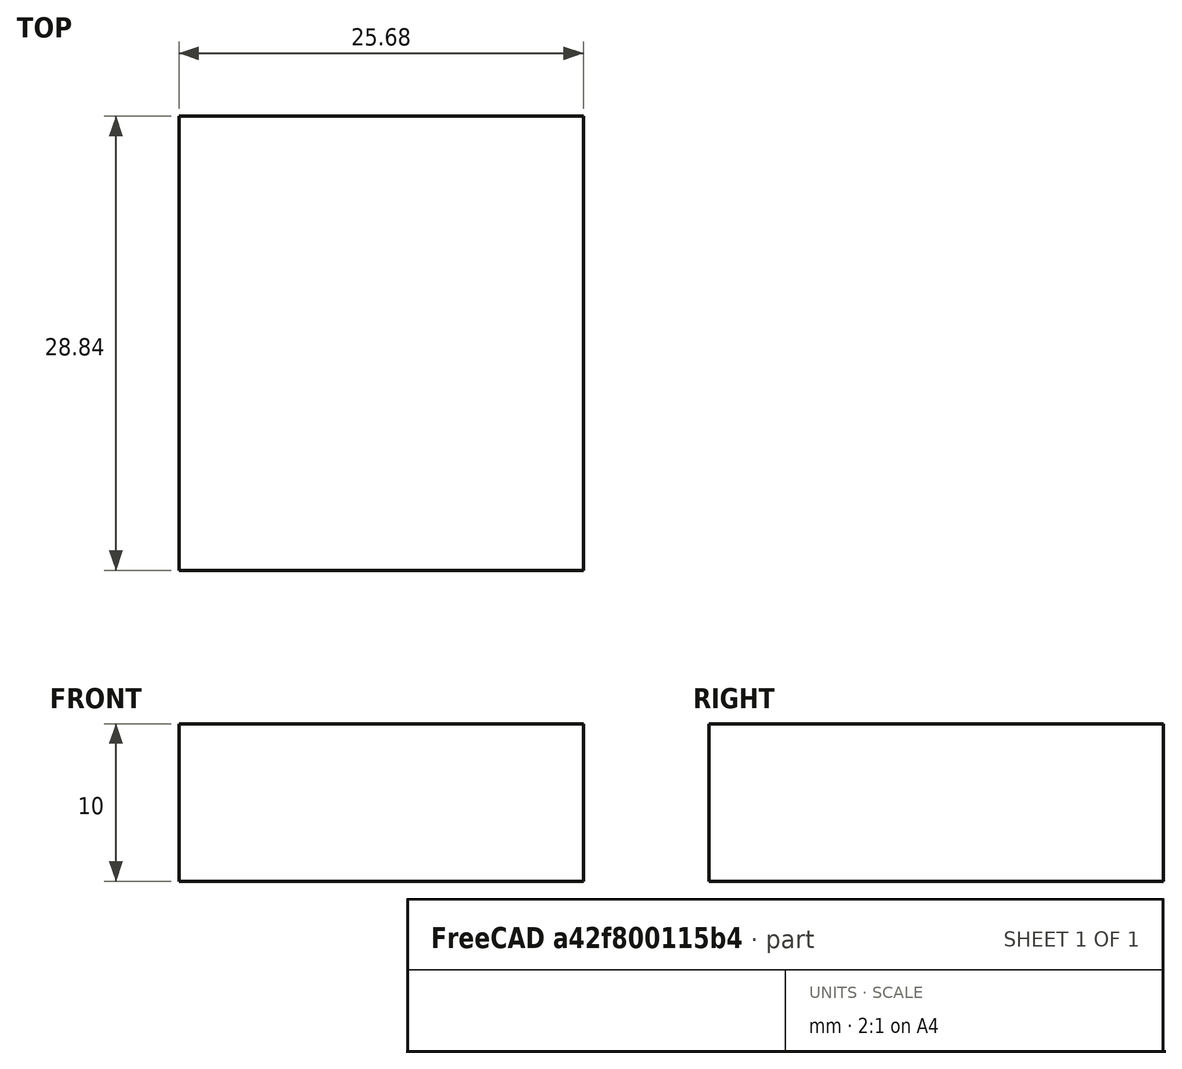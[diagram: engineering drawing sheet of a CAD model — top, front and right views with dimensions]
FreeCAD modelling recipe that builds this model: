
FCSTD DOCUMENT  (FreeCAD 1.1R14555 (Git shallow))
Label: TestInsertLink1-1
License: All rights reserved
LicenseURL: https://en.wikipedia.org/wiki/All_rights_reserved
objects: App::Link×8, App::Point×4, Assembly::AssemblyLink×2, App::FeaturePython×2, Sketcher::SketchObject×1, PartDesign::Pad×1, PartDesign::Body×1, Assembly::JointGroup×1, Assembly::AssemblyObject×1
note: 6 computed .brp shape members not serialized (recipe doc carries the construction recipe); baked Part::Feature solids carry a one-line shape summary decoded from their .brp
EXTERNAL_REF file=TestMeca1-1.FCStd obj=Assembly
EXTERNAL_REF file=TestMeca1-1.FCStd obj=Body
EXTERNAL_REF file=TestMeca1-1.FCStd obj=Body001
EXTERNAL_REF file=TestMeca1-1.FCStd obj=Body002
EXTERNAL_REF file=TestMeca1-1.FCStd obj=Body004
EXTERNAL_REF file=TestMeca1-1.FCStd obj=Body005
EXTERNAL_REF file=TestMeca1-1.FCStd obj=Assembly001
EXTERNAL_REF file=TestMeca1-1.FCStd obj=Assembly002
EXTERNAL_REF file=TestInsert1-1.FCStd obj=Body
EXTERNAL_REF file=TestInsert1-1.FCStd obj=Body001

FEATURE [App::Point] Origin001  label="Origine"
  Role = Origin
FEATURE [App::Point] Origin003  label="Origine002"
  Role = Origin
FEATURE [App::Link] Body  label="Corps"
  LinkedObject = -> <external TestMeca1-1.FCStd>#Body
FEATURE [App::Link] Body001  label="Corps001"
  LinkPlacement = pos=(-5.08123,5,5.38487) rot=(0,1,0;0.743384rad)
  LinkedObject = -> <external TestMeca1-1.FCStd>#Body001
  Placement = pos=(-5.08123,5,5.38487) rot=(0,1,0;0.743384rad)
FEATURE [App::Link] Body002  label="Corps002"
  LinkPlacement = pos=(67.6695,10,-11.2681) rot=(0,-1,0;0.15337rad)
  LinkedObject = -> <external TestMeca1-1.FCStd>#Body002
  Placement = pos=(67.6695,10,-11.2681) rot=(0,-1,0;0.15337rad)
FEATURE [App::Link] Body004  label="Corps004"
  LinkPlacement = pos=(40.5944,10,0.68856) rot=(0,-1,0;0.161439rad)
  LinkedObject = -> <external TestMeca1-1.FCStd>#Body004
  Placement = pos=(40.5944,10,0.68856) rot=(0,-1,0;0.161439rad)
FEATURE [App::Link] Body005  label="Corps005"
  LinkPlacement = pos=(5.56671,5,23.7456) rot=(0,1,0;0.882835rad)
  LinkedObject = -> <external TestMeca1-1.FCStd>#Body005
  Placement = pos=(5.56671,5,23.7456) rot=(0,1,0;0.882835rad)
FEATURE [App::Link] Assembly002  label="Assembly001"
  LinkPlacement = pos=(-34.0984,5.00001,62.3122) rot=(0,1,0;0.514812rad)
  LinkedObject = -> <external TestMeca1-1.FCStd>#Assembly001
  Placement = pos=(-34.0984,5.00001,62.3122) rot=(0,1,0;0.514812rad)
FEATURE [App::Point] Origin005  label="Origine004"
  Role = Origin
FEATURE [App::Link] Body006  label="Corps006"
  LinkedObject = -> <external TestInsert1-1.FCStd>#Body
FEATURE [App::Link] Body007  label="Corps007"
  LinkPlacement = pos=(-4.1e-15,3.6e-15,-4.7e-15) rot=(0,-1,0;4.71239rad)
  LinkedObject = -> <external TestInsert1-1.FCStd>#Body001
  Placement = pos=(-4.1e-15,3.6e-15,-4.7e-15) rot=(0,-1,0;4.71239rad)
FEATURE [Assembly::AssemblyLink] Assembly003  label="Assembly"
  Group = -> [Body006,Body007]
  LinkedObject = -> <external TestMeca1-1.FCStd>#Assembly002
  Origin = -> Origin004
  Placement = pos=(76.0304,-8,33.5737) rot=(0,1,0;0.730396rad)
  Rigid = true
FEATURE [Assembly::AssemblyLink] Assembly001  label="Assembly"
  Group = -> [Body,Body001,Body002,Body004,Body005,Assembly002,Assembly003]
  LinkedObject = -> <external TestMeca1-1.FCStd>#Assembly
  Origin = -> Origin002
  Placement = pos=(13.8231,8.63205,0) rot=(0,0,1;3.85382rad)
  Rigid = true
FEATURE [App::Point] Origin007  label="Origine006"
  Role = Origin
FEATURE [Sketcher::SketchObject] Sketch
  ArcFitTolerance = 1e-06
  AttachmentSupport = -> [Origin006]
  ExternalTypes = [0]
  FullyConstrained = false
  MakeInternals = false
  MapMode = 5
  sketch-geometry (5):
    g0: LineSegment StartX=12.8432 StartY=-14.4217 StartZ=0 EndX=12.8432 EndY=14.4217 EndZ=0
    g1: LineSegment StartX=12.8432 StartY=14.4217 StartZ=0 EndX=-12.8432 EndY=14.4217 EndZ=0
    g2: LineSegment StartX=-12.8432 StartY=14.4217 StartZ=0 EndX=-12.8432 EndY=-14.4217 EndZ=0
    g3: LineSegment StartX=-12.8432 StartY=-14.4217 StartZ=0 EndX=12.8432 EndY=-14.4217 EndZ=0
    g4: GeomPoint [constr] X=0 Y=0 Z=0
  constraints (10):
    c: Coincident(g0,g1)
    c: Coincident(g1,g2)
    c: Coincident(g2,g3)
    c: Coincident(g3,g0)
    c: Vertical(g0)
    c: Vertical(g2)
    c: Horizontal(g1)
    c: Horizontal(g3)
    c: Symmetric(g2,g0,g4)
    c: Coincident(g4,g-1)
FEATURE [PartDesign::Pad] Pad
  Direction = (0,0,1)
  Length = 10
  Length2 = 10
  Profile = -> Sketch
  ReferenceAxis = -> Sketch [N_Axis]
  Refine = true
  Reversed = true
  SideType = 0
  Suppressed = false
  Type = 0
  Type2 = 0
FEATURE [PartDesign::Body] Body008  label="Corps008"
  AllowCompound = false
  Group = -> [Sketch,Pad]
  Origin = -> Origin006
  Tip = -> Pad
FEATURE [App::FeaturePython] GroundedJoint  # Assembly grounded joint (typed FeaturePython)
  ObjectToGround = -> Body008
FEATURE [App::FeaturePython] Joint  label="Revolute"  # Assembly joint (typed FeaturePython)
  Angle = 0
  AngleMax = 0
  AngleMin = 0
  Detach1 = false
  Detach2 = false
  Distance = 0
  Distance2 = 0
  EnableAngleMax = false
  EnableAngleMin = false
  EnableLengthMax = false
  EnableLengthMin = false
  JointType = 1 (Revolute)
  LengthMax = 0
  LengthMin = 0
  Placement1 = pos=(-1e-16,0,0) rot=(0,0,1;0rad)
  Placement2 = pos=(16.1041,-2.5,6e-16) rot=(0,1,0;3.14159rad)
  Reference1 = -> Assembly [Body008.Face5,Body008.Face5]
  Reference2 = -> Assembly [Assembly001.Body.Face4,Assembly001.Body.Face4]
  Suppressed = false
FEATURE [Assembly::JointGroup] Joints
  Group = -> [GroundedJoint,Joint]
FEATURE [Assembly::AssemblyObject] Assembly
  Group = -> [Joints,Assembly001,Body008,GroundedJoint,Joint]
  Origin = -> Origin
  Type = Assembly

RESOLVED EXTERNAL PARTS (link-assembly join: the EXTERNAL_REF files above that resolve inside this repo's crawl, each included once):
---- part TestInsert1-1.FCStd = doc fcstd_bb9fa522eb82 ----
FCSTD DOCUMENT  (FreeCAD 1.1R14555 (Git shallow))
Label: TestInsert1-1
License: All rights reserved
LicenseURL: https://en.wikipedia.org/wiki/All_rights_reserved
objects: App::Point×3, Sketcher::SketchObject×2, PartDesign::Pad×2, PartDesign::Body×2, App::FeaturePython×1, Assembly::JointGroup×1, Assembly::AssemblyObject×1
note: 12 computed .brp shape members not serialized (recipe doc carries the construction recipe); baked Part::Feature solids carry a one-line shape summary decoded from their .brp

FEATURE [App::Point] Origin001  label="Origine"
  Role = Origin
FEATURE [App::Point] Origin003  label="Origine002"
  Role = Origin
FEATURE [Sketcher::SketchObject] Sketch
  ArcFitTolerance = 1e-06
  AttachmentSupport = -> [Origin002]
  ExternalTypes = [0]
  FullyConstrained = false
  MakeInternals = false
  MapMode = 5
  Placement = pos=(0,0,0) rot=(1,0,0;1.5708rad)
  sketch-geometry (4):
    g0: ArcOfCircle CenterX=0 CenterY=0 CenterZ=0 NormalX=0 NormalY=0 NormalZ=1 AngleXU=0 Radius=3.30838 StartAngle=2.28574 EndAngle=5.42733
    g1: ArcOfCircle CenterX=11.4427 CenterY=9.93411 CenterZ=0 NormalX=0 NormalY=0 NormalZ=1 AngleXU=0 Radius=3.30838 StartAngle=5.42733 EndAngle=8.56893
    g2: LineSegment StartX=-2.1689 StartY=2.49826 StartZ=0 EndX=9.27378 EndY=12.4324 EndZ=0
    g3: LineSegment StartX=2.1689 StartY=-2.49826 StartZ=0 EndX=13.6116 EndY=7.43585 EndZ=0
  constraints (6):
    c: Tangent(g0,g2) = 1.5708
    c: Tangent(g0,g3) = -1.5708
    c: Tangent(g1,g2) = 1.5708
    c: Tangent(g1,g3) = -1.5708
    c: Equal(g0,g1)
    c: Coincident(g0,g-1)
FEATURE [PartDesign::Pad] Pad
  Direction = (0,-1,0)
  Length = 10
  Length2 = 10
  Profile = -> Sketch
  ReferenceAxis = -> Sketch [N_Axis]
  Refine = true
  SideType = 0
  Suppressed = false
  Type = 0
  Type2 = 0
FEATURE [PartDesign::Body] Body  label="Corps"
  AllowCompound = false
  Group = -> [Sketch,Pad]
  Origin = -> Origin002
  Tip = -> Pad
FEATURE [App::Point] Origin005  label="Origine004"
  Role = Origin
FEATURE [Sketcher::SketchObject] Sketch001
  ArcFitTolerance = 1e-06
  AttachmentSupport = -> [Origin004]
  ExternalTypes = [0]
  FullyConstrained = false
  MakeInternals = false
  MapMode = 5
  Placement = pos=(0,0,0) rot=(1,0,0;1.5708rad)
  sketch-geometry (1):
    g0: Circle CenterX=0 CenterY=0 CenterZ=0 NormalX=0 NormalY=0 NormalZ=1 AngleXU=0 Radius=7.06658
  constraints (1):
    c: Coincident(g0,g-1)
FEATURE [PartDesign::Pad] Pad001
  Direction = (0,-1,0)
  Length = 10
  Length2 = 10
  Profile = -> Sketch001
  ReferenceAxis = -> Sketch001 [N_Axis]
  Refine = true
  SideType = 0
  Suppressed = false
  Type = 0
  Type2 = 0
FEATURE [PartDesign::Body] Body001  label="Corps001"
  AllowCompound = false
  Group = -> [Sketch001,Pad001]
  Origin = -> Origin004
  Placement = pos=(-4.1e-15,3.6e-15,-4.7e-15) rot=(0,-1,0;4.71239rad)
  Tip = -> Pad001
FEATURE [App::FeaturePython] Joint  label="Fixed"  # Assembly joint (typed FeaturePython)
  Angle = 0
  AngleMax = 0
  AngleMin = 0
  Detach1 = false
  Detach2 = false
  Distance = 0
  Distance2 = 0
  EnableAngleMax = false
  EnableAngleMin = false
  EnableLengthMax = false
  EnableLengthMin = false
  JointType = 0 (Fixed)
  LengthMax = 0
  LengthMin = 0
  Placement1 = pos=(9e-16,-10,2.2e-15) rot=(0.57735,0.57735,0.57735;4.18879rad)
  Placement2 = pos=(0,-10,2.2e-15) rot=(1,0,0;1.5708rad)
  Reference1 = -> Assembly [Body001.Face3,Body001.Face3]
  Reference2 = -> Assembly [Body.Edge4,Body.Edge4]
  Suppressed = false
FEATURE [Assembly::JointGroup] Joints
  Group = -> [Joint]
FEATURE [Assembly::AssemblyObject] Assembly
  Group = -> [Joints,Body,Body001,Joint]
  Origin = -> Origin
  Type = Assembly
---- part TestMeca1-1.FCStd = doc fcstd_c90dfbcddba9 ----
FCSTD DOCUMENT  (FreeCAD 1.1R14555 (Git shallow))
Label: TestMeca1-1
License: All rights reserved
LicenseURL: https://en.wikipedia.org/wiki/All_rights_reserved
objects: App::Point×11, App::FeaturePython×10, Sketcher::SketchObject×7, PartDesign::Pad×7, PartDesign::Body×7, App::Link×4, Assembly::JointGroup×2, Assembly::AssemblyObject×2, Image::ImagePlane×1, App::Part×1, Assembly::AssemblyLink×1
note: 42 computed .brp shape members not serialized (recipe doc carries the construction recipe); baked Part::Feature solids carry a one-line shape summary decoded from their .brp
EXTERNAL_REF file=TestInsert1-1.FCStd obj=Assembly
EXTERNAL_REF file=TestInsert1-1.FCStd obj=Body
EXTERNAL_REF file=TestInsert1-1.FCStd obj=Body001

FEATURE [App::Point] Origin001  label="Origine"
  Role = Origin
FEATURE [Image::ImagePlane] GN_7247_Charnière_articulée_drawing  label="GN 7247-Charnière articulée-drawing"
  Placement = pos=(-46,0,-26) rot=(1,0,0;1.5708rad)
  XSize = 264.55
  YSize = 264.55
FEATURE [App::Point] Origin003  label="Origine002"
  Role = Origin
FEATURE [Sketcher::SketchObject] Sketch
  ArcFitTolerance = 1e-06
  AttachmentSupport = -> [Origin002]
  ExternalTypes = [0]
  FullyConstrained = false
  MakeInternals = false
  MapMode = 5
  Placement = pos=(0,0,0) rot=(1,0,0;1.5708rad)
  sketch-geometry (6):
    g0: LineSegment StartX=0 StartY=0 StartZ=0 EndX=0 EndY=13.138 EndZ=0
    g1: LineSegment StartX=0 StartY=13.138 StartZ=0 EndX=32.2081 EndY=10.2743 EndZ=0
    g2: LineSegment StartX=32.2081 StartY=10.2743 StartZ=0 EndX=32.2081 EndY=0 EndZ=0
    g3: LineSegment StartX=32.2081 StartY=0 StartZ=0 EndX=0 EndY=0 EndZ=0
    g4: Circle CenterX=27.9622 CenterY=5.98985 CenterZ=0 NormalX=0 NormalY=0 NormalZ=1 AngleXU=0 Radius=2.08292
    g5: Circle CenterX=4.43862 CenterY=9.24882 CenterZ=0 NormalX=0 NormalY=0 NormalZ=1 AngleXU=0 Radius=2.03403
  constraints (8):
    c: Coincident(g-1,g0)
    c: PointOnObject(g0,g-2)
    c: Coincident(g0,g1)
    c: Coincident(g1,g2)
    c: PointOnObject(g2,g-1)
    c: Vertical(g2)
    c: Coincident(g2,g3)
    c: Coincident(g3,g0)
FEATURE [PartDesign::Pad] Pad
  Direction = (0,-1,0)
  Length = 5
  Length2 = 10
  Profile = -> Sketch
  ReferenceAxis = -> Sketch [N_Axis]
  Refine = true
  SideType = 0
  Suppressed = false
  Type = 0
  Type2 = 0
FEATURE [PartDesign::Body] Body  label="Corps"
  AllowCompound = false
  Group = -> [Sketch,Pad]
  Origin = -> Origin002
  Tip = -> Pad
FEATURE [App::Point] Origin005  label="Origine004"
  Role = Origin
FEATURE [Sketcher::SketchObject] Sketch001
  ArcFitTolerance = 1e-06
  AttachmentSupport = -> [Origin004]
  ExternalTypes = [0]
  FullyConstrained = false
  MakeInternals = false
  MapMode = 5
  Placement = pos=(0,0,0) rot=(1,0,0;1.5708rad)
  sketch-geometry (6):
    g0: ArcOfCircle CenterX=4.3933 CenterY=9.28745 CenterZ=0 NormalX=0 NormalY=0 NormalZ=1 AngleXU=0 Radius=3.55115 StartAngle=3.65377 EndAngle=6.79537
    g1: ArcOfCircle CenterX=-16.3679 CenterY=46.2142 CenterZ=0 NormalX=0 NormalY=0 NormalZ=1 AngleXU=0 Radius=3.55115 StartAngle=0.512182 EndAngle=3.65377
    g2: LineSegment StartX=1.29784 StartY=7.5471 StartZ=0 EndX=-19.4634 EndY=44.4739 EndZ=0
    g3: LineSegment StartX=7.48876 StartY=11.0278 StartZ=0 EndX=-13.2724 EndY=47.9545 EndZ=0
    g4: Circle CenterX=-16.3679 CenterY=46.2142 CenterZ=0 NormalX=0 NormalY=0 NormalZ=1 AngleXU=0 Radius=1.89824
    g5: Circle CenterX=4.3933 CenterY=9.28745 CenterZ=0 NormalX=0 NormalY=0 NormalZ=1 AngleXU=0 Radius=1.85066
  constraints (7):
    c: Tangent(g0,g2) = 1.5708
    c: Tangent(g0,g3) = -1.5708
    c: Tangent(g1,g2) = 1.5708
    c: Tangent(g1,g3) = -1.5708
    c: Equal(g0,g1)
    c: Coincident(g4,g1)
    c: Coincident(g5,g0)
FEATURE [PartDesign::Pad] Pad001
  Direction = (0,-1,2e-16)
  Length = 5
  Length2 = 10
  Profile = -> Sketch001
  ReferenceAxis = -> Sketch001 [N_Axis]
  Refine = true
  SideType = 0
  Suppressed = false
  Type = 0
  Type2 = 0
FEATURE [PartDesign::Body] Body001  label="Corps001"
  AllowCompound = false
  Group = -> [Sketch001,Pad001]
  Origin = -> Origin004
  Placement = pos=(-5.49004,5,6.60695) rot=(0,1,0;0.868892rad)
  Tip = -> Pad001
FEATURE [App::Point] Origin007  label="Origine006"
  Role = Origin
FEATURE [Sketcher::SketchObject] Sketch002
  ArcFitTolerance = 1e-06
  AttachmentSupport = -> [Origin006]
  ExternalTypes = [0]
  FullyConstrained = false
  MakeInternals = false
  MapMode = 5
  Placement = pos=(0,0,0) rot=(1,0,0;1.5708rad)
  sketch-geometry (6):
    g0: ArcOfCircle CenterX=9.93968 CenterY=74.2901 CenterZ=0 NormalX=0 NormalY=0 NormalZ=1 AngleXU=0 Radius=3.51304 StartAngle=0.499119 EndAngle=3.64071
    g1: ArcOfCircle CenterX=22.1303 CenterY=51.9285 CenterZ=0 NormalX=0 NormalY=0 NormalZ=1 AngleXU=0 Radius=3.51304 StartAngle=3.64071 EndAngle=6.7823
    g2: LineSegment StartX=13.0241 StartY=75.9716 StartZ=0 EndX=25.2148 EndY=53.61 EndZ=0
    g3: LineSegment StartX=6.85522 StartY=72.6086 StartZ=0 EndX=19.0458 EndY=50.247 EndZ=0
    g4: Circle CenterX=9.93968 CenterY=74.2901 CenterZ=0 NormalX=0 NormalY=0 NormalZ=1 AngleXU=0 Radius=2.12816
    g5: Circle CenterX=22.1303 CenterY=51.9285 CenterZ=0 NormalX=0 NormalY=0 NormalZ=1 AngleXU=0 Radius=2.08513
  constraints (7):
    c: Tangent(g0,g2) = 1.5708
    c: Tangent(g0,g3) = -1.5708
    c: Tangent(g1,g2) = 1.5708
    c: Tangent(g1,g3) = -1.5708
    c: Equal(g0,g1)
    c: Coincident(g4,g0)
    c: Coincident(g5,g1)
FEATURE [PartDesign::Pad] Pad002
  Direction = (0,-1,2e-16)
  Length = 5
  Length2 = 10
  Profile = -> Sketch002
  ReferenceAxis = -> Sketch002 [N_Axis]
  Refine = true
  SideType = 0
  Suppressed = false
  Type = 0
  Type2 = 0
FEATURE [PartDesign::Body] Body002  label="Corps002"
  AllowCompound = false
  Group = -> [Sketch002,Pad002]
  Origin = -> Origin006
  Placement = pos=(75.9415,10,-16.972) rot=(0,-1,0;0.16388rad)
  Tip = -> Pad002
FEATURE [App::Point] Origin009  label="Origine008"
  Role = Origin
FEATURE [Sketcher::SketchObject] Sketch003
  ArcFitTolerance = 1e-06
  AttachmentSupport = -> [Origin008]
  ExternalTypes = [0]
  FullyConstrained = false
  MakeInternals = false
  MapMode = 5
  Placement = pos=(0,0,0) rot=(1,0,0;1.5708rad)
  sketch-geometry (6):
    g0: ArcOfCircle CenterX=33.0045 CenterY=40.5366 CenterZ=0 NormalX=0 NormalY=0 NormalZ=1 AngleXU=0 Radius=4.15593 StartAngle=1e-16 EndAngle=3.14159
    g1: ArcOfCircle CenterX=33.0045 CenterY=17.7064 CenterZ=0 NormalX=0 NormalY=0 NormalZ=1 AngleXU=0 Radius=4.15593 StartAngle=3.14159 EndAngle=6.28319
    g2: LineSegment StartX=37.1605 StartY=40.5366 StartZ=0 EndX=37.1605 EndY=17.7064 EndZ=0
    g3: LineSegment StartX=28.8486 StartY=40.5366 StartZ=0 EndX=28.8486 EndY=17.7064 EndZ=0
    g4: Circle CenterX=33.0045 CenterY=40.5366 CenterZ=0 NormalX=0 NormalY=0 NormalZ=1 AngleXU=0 Radius=2.09794
    g5: Circle CenterX=33.0045 CenterY=17.7064 CenterZ=0 NormalX=0 NormalY=0 NormalZ=1 AngleXU=0 Radius=2.22145
  constraints (8):
    c: Tangent(g0,g2) = 1.5708
    c: Tangent(g0,g3) = -1.5708
    c: Tangent(g1,g2) = 1.5708
    c: Tangent(g1,g3) = -1.5708
    c: Equal(g0,g1)
    c: Vertical(g2)
    c: Coincident(g4,g0)
    c: Coincident(g5,g1)
FEATURE [PartDesign::Pad] Pad003
  Direction = (0,-1,0)
  Length = 5
  Length2 = 10
  Profile = -> Sketch003
  ReferenceAxis = -> Sketch003 [N_Axis]
  Refine = true
  SideType = 0
  Suppressed = false
  Type = 0
  Type2 = 0
FEATURE [PartDesign::Body] Body003  label="Corps003"
  AllowCompound = false
  Group = -> [Sketch003,Pad003]
  Origin = -> Origin008
  Placement = pos=(46.8816,15,31.1819) rot=(0,1,0;0.962596rad)
  Tip = -> Pad003
FEATURE [App::Point] Origin011  label="Origine010"
  Role = Origin
FEATURE [Sketcher::SketchObject] Sketch004
  ArcFitTolerance = 1e-06
  AttachmentSupport = -> [Origin010]
  ExternalTypes = [0]
  FullyConstrained = false
  MakeInternals = false
  MapMode = 5
  Placement = pos=(0,0,0) rot=(1,0,0;1.5708rad)
  sketch-geometry (10):
    g0: LineSegment StartX=-23.6072 StartY=51.3966 StartZ=0 EndX=-21.2757 EndY=58.8351 EndZ=0
    g1: LineSegment StartX=-21.2757 StartY=58.8351 StartZ=0 EndX=14.4735 EndY=44.1801 EndZ=0
    g2: LineSegment StartX=14.4735 StartY=44.1801 StartZ=0 EndX=37.011 EndY=26.9717 EndZ=0
    g3: LineSegment StartX=37.011 StartY=26.9717 StartZ=0 EndX=37.011 EndY=14.5372 EndZ=0
    g4: LineSegment StartX=37.011 StartY=14.5372 StartZ=0 EndX=29.2394 EndY=14.8702 EndZ=0
    g5: LineSegment StartX=29.2394 StartY=14.8702 StartZ=0 EndX=29.2394 EndY=25.3063 EndZ=0
    g6: LineSegment StartX=29.2394 StartY=25.3063 StartZ=0 EndX=-23.6072 EndY=51.3966 EndZ=0
    g7: Circle CenterX=33.061 CenterY=17.7892 CenterZ=0 NormalX=0 NormalY=0 NormalZ=1 AngleXU=0 Radius=1.92887
    g8: Circle CenterX=9.13695 CenterY=41.0232 CenterZ=0 NormalX=0 NormalY=0 NormalZ=1 AngleXU=0 Radius=1.9865
    g9: Circle CenterX=-18.1003 CenterY=53.3997 CenterZ=0 NormalX=0 NormalY=0 NormalZ=1 AngleXU=0 Radius=1.8317
  constraints (9):
    c: Coincident(g0,g1)
    c: Coincident(g1,g2)
    c: Coincident(g2,g3)
    c: Vertical(g3)
    c: Coincident(g3,g4)
    c: Coincident(g4,g5)
    c: Vertical(g5)
    c: Coincident(g5,g6)
    c: Coincident(g6,g0)
FEATURE [PartDesign::Pad] Pad004
  Direction = (0,-1,0)
  Length = 5
  Length2 = 10
  Profile = -> Sketch004
  ReferenceAxis = -> Sketch004 [N_Axis]
  Refine = true
  SideType = 0
  Suppressed = false
  Type = 0
  Type2 = 0
FEATURE [PartDesign::Body] Body004  label="Corps004"
  AllowCompound = false
  Group = -> [Sketch004,Pad004]
  Origin = -> Origin010
  Placement = pos=(44.202,10,-1.60818) rot=(0,-1,0;0.131988rad)
  Tip = -> Pad004
FEATURE [App::Point] Origin013  label="Origine012"
  Role = Origin
FEATURE [Sketcher::SketchObject] Sketch005
  ArcFitTolerance = 1e-06
  AttachmentSupport = -> [Origin012]
  ExternalTypes = [0]
  FullyConstrained = false
  MakeInternals = false
  MapMode = 5
  Placement = pos=(0,0,0) rot=(1,0,0;1.5708rad)
  sketch-geometry (11):
    g0: LineSegment StartX=3.31041 StartY=76.0954 StartZ=0 EndX=11.193 EndY=76.0954 EndZ=0
    g1: LineSegment StartX=11.193 StartY=76.0954 StartZ=0 EndX=13.8575 EndY=22.0275 EndZ=0
    g2: LineSegment StartX=13.8575 StartY=22.0275 StartZ=0 EndX=25.3278 EndY=10.0553 EndZ=0
    g3: LineSegment StartX=25.3278 StartY=10.0553 StartZ=0 EndX=32.1894 EndY=9.81025 EndZ=0
    g4: LineSegment StartX=32.1894 StartY=9.81025 StartZ=0 EndX=32.1894 EndY=2.90781 EndZ=0
    g5: LineSegment StartX=32.1894 StartY=2.90781 StartZ=0 EndX=20.7126 EndY=2.90781 EndZ=0
    g6: LineSegment StartX=20.7126 StartY=2.90781 StartZ=0 EndX=6.25418 EndY=19.1224 EndZ=0
    g7: LineSegment StartX=6.25418 StartY=19.1224 StartZ=0 EndX=3.31041 EndY=76.0954 EndZ=0
    g8: Circle CenterX=7.62181 CenterY=72.1475 CenterZ=0 NormalX=0 NormalY=0 NormalZ=1 AngleXU=0 Radius=1.96538
    g9: Circle CenterX=9.17842 CenterY=40.9348 CenterZ=0 NormalX=0 NormalY=0 NormalZ=1 AngleXU=0 Radius=1.89735
    g10: Circle CenterX=27.9374 CenterY=6.02718 CenterZ=0 NormalX=0 NormalY=0 NormalZ=1 AngleXU=0 Radius=1.89735
  constraints (11):
    c: Horizontal(g0)
    c: Coincident(g0,g1)
    c: Coincident(g1,g2)
    c: Coincident(g2,g3)
    c: Coincident(g3,g4)
    c: Vertical(g4)
    c: Coincident(g4,g5)
    c: Horizontal(g5)
    c: Coincident(g5,g6)
    c: Coincident(g6,g7)
    c: Coincident(g7,g0)
FEATURE [PartDesign::Pad] Pad005
  Direction = (0,-1,0)
  Length = 5
  Length2 = 10
  Profile = -> Sketch005
  ReferenceAxis = -> Sketch005 [N_Axis]
  Refine = true
  SideType = 0
  Suppressed = false
  Type = 0
  Type2 = 0
FEATURE [PartDesign::Body] Body005  label="Corps005"
  AllowCompound = false
  Group = -> [Sketch005,Pad005]
  Origin = -> Origin012
  Placement = pos=(8.18757,5,26.6245) rot=(0,1,0;1.01916rad)
  Tip = -> Pad005
FEATURE [App::FeaturePython] GroundedJoint  # Assembly grounded joint (typed FeaturePython)
  ObjectToGround = -> Body
FEATURE [App::FeaturePython] Joint  label="Revolute"  # Assembly joint (typed FeaturePython)
  Angle = 0
  AngleMax = 0
  AngleMin = 0
  Detach1 = false
  Detach2 = false
  Distance = 0
  Distance2 = 0
  EnableAngleMax = false
  EnableAngleMin = false
  EnableLengthMax = false
  EnableLengthMin = false
  JointType = 1 (Revolute)
  LengthMax = 0
  LengthMin = 0
  Placement1 = pos=(4.3933,-5,9.28745) rot=(1,0,0;1.5708rad)
  Placement2 = pos=(4.43862,0,9.24882) rot=(1,0,0;1.5708rad)
  Reference1 = -> Assembly [Body001.Edge18,Body001.Edge18]
  Reference2 = -> Assembly [Body.Edge17,Body.Edge17]
  Suppressed = false
FEATURE [App::FeaturePython] Joint001  label="Revolute001"  # Assembly joint (typed FeaturePython)
  Angle = 0
  AngleMax = 0
  AngleMin = 0
  Detach1 = false
  Detach2 = false
  Distance = 0
  Distance2 = 0
  EnableAngleMax = false
  EnableAngleMin = false
  EnableLengthMax = false
  EnableLengthMin = false
  JointType = 1 (Revolute)
  LengthMax = 0
  LengthMin = 0
  Placement1 = pos=(-16.3679,0,46.2142) rot=(1,0,0;1.5708rad)
  Placement2 = pos=(-18.1003,-5,53.3997) rot=(1,0,0;1.5708rad)
  Reference1 = -> Assembly [Body001.Edge14,Body001.Edge14]
  Reference2 = -> Assembly [Body004.Edge30,Body004.Edge30]
  Suppressed = false
FEATURE [App::FeaturePython] Joint002  label="Revolute002"  # Assembly joint (typed FeaturePython)
  Angle = 0
  AngleMax = 0
  AngleMin = 0
  Detach1 = false
  Detach2 = false
  Distance = 0
  Distance2 = 0
  EnableAngleMax = false
  EnableAngleMin = false
  EnableLengthMax = false
  EnableLengthMin = false
  JointType = 1 (Revolute)
  LengthMax = 0
  LengthMin = 0
  Placement1 = pos=(27.9374,-5,6.02718) rot=(1,0,0;1.5708rad)
  Placement2 = pos=(27.9622,0,5.98985) rot=(1,0,0;1.5708rad)
  Reference1 = -> Assembly [Body005.Edge33,Body005.Edge33]
  Reference2 = -> Assembly [Body.Edge14,Body.Edge14]
  Suppressed = false
FEATURE [App::FeaturePython] Joint005  label="Revolute005"  # Assembly joint (typed FeaturePython)
  Angle = 0
  AngleMax = 0
  AngleMin = 0
  Detach1 = false
  Detach2 = false
  Distance = 0
  Distance2 = 0
  EnableAngleMax = false
  EnableAngleMin = false
  EnableLengthMax = false
  EnableLengthMin = false
  JointType = 1 (Revolute)
  LengthMax = 0
  LengthMin = 0
  Placement1 = pos=(9.93968,-5,74.2901) rot=(1,0,0;1.5708rad)
  Placement2 = pos=(7.62181,0,72.1475) rot=(1,0,0;1.5708rad)
  Reference1 = -> Assembly [Body002.Edge15,Body002.Edge15]
  Reference2 = -> Assembly [Body005.Edge26,Body005.Edge26]
  Suppressed = false
FEATURE [App::FeaturePython] Joint006  label="Revolute006"  # Assembly joint (typed FeaturePython)
  Angle = 0
  AngleMax = 0
  AngleMin = 0
  Detach1 = false
  Detach2 = false
  Distance = 0
  Distance2 = 0
  EnableAngleMax = false
  EnableAngleMin = false
  EnableLengthMax = false
  EnableLengthMin = false
  JointType = 1 (Revolute)
  LengthMax = 0
  LengthMin = 0
  Placement1 = pos=(9.13695,-5,41.0232) rot=(1,0,0;1.5708rad)
  Placement2 = pos=(9.17842,0,40.9348) rot=(1,0,0;1.5708rad)
  Reference1 = -> Assembly [Body004.Edge24,Body004.Edge24]
  Reference2 = -> Assembly [Body005.Edge29,Body005.Edge29]
  Suppressed = false
FEATURE [App::Point] Origin015  label="Origine014"
  Role = Origin
FEATURE [App::Point] Origin017  label="Origine016"
  Role = Origin
FEATURE [Sketcher::SketchObject] Sketch006
  ArcFitTolerance = 1e-06
  AttachmentSupport = -> [Origin016]
  ExternalTypes = [0]
  FullyConstrained = false
  MakeInternals = false
  MapMode = 5
  Placement = pos=(0,0,0) rot=(1,0,0;1.5708rad)
  sketch-geometry (1):
    g0: Circle CenterX=95.172 CenterY=14.315 CenterZ=0 NormalX=0 NormalY=0 NormalZ=1 AngleXU=0 Radius=5.91026
FEATURE [PartDesign::Pad] Pad006
  Direction = (0,-1,2e-16)
  Length = 23
  Length2 = 10
  Profile = -> Sketch006
  ReferenceAxis = -> Sketch006 [N_Axis]
  Refine = true
  Reversed = true
  SideType = 0
  Suppressed = false
  Type = 0
  Type2 = 0
FEATURE [PartDesign::Body] Body006  label="Corps006"
  AllowCompound = false
  Group = -> [Sketch006,Pad006]
  Origin = -> Origin016
  Tip = -> Pad006
FEATURE [App::Part] Part
  Group = -> [Body003,Body006]
  Origin = -> Origin014
FEATURE [App::Point] Origin019  label="Origine018"
  Role = Origin
FEATURE [App::Link] Corps003
  LinkPlacement = pos=(77,-8.82149e-06,-4.76837e-07) rot=(0,0,1;0rad)
  LinkedObject = -> Body003
  Placement = pos=(77,-8.82149e-06,-4.76837e-07) rot=(0,0,1;0rad)
FEATURE [App::Link] Corps006
  LinkPlacement = pos=(14.8325,-13,14.8956) rot=(0,0,1;0rad)
  LinkedObject = -> Body006
  Placement = pos=(14.8325,-13,14.8956) rot=(0,0,1;0rad)
FEATURE [App::FeaturePython] Joint007  label="Fixed001"  # Assembly joint (typed FeaturePython)
  Angle = 0
  AngleMax = 0
  AngleMin = 0
  Detach1 = false
  Detach2 = false
  Distance = 0
  Distance2 = 0
  EnableAngleMax = false
  EnableAngleMin = false
  EnableLengthMax = false
  EnableLengthMin = false
  JointType = 0 (Fixed)
  LengthMax = 0
  LengthMin = 0
  Offset2 = pos=(0,0,-8) rot=(0,0,1;0rad)
  Placement1 = pos=(95.172,3.6e-15,14.315) rot=(0.57735,0.57735,0.57735;4.18879rad)
  Placement2 = pos=(33.0045,-13,29.2106) rot=(0.57735,0.57735,0.57735;4.18879rad)
  Reference1 = -> Assembly [Assembly001.Corps006.Face2,Assembly001.Corps006.Face2]
  Reference2 = -> Assembly [Assembly001.Corps003.Face8,Assembly001.Corps003.Face8]
  Suppressed = false
FEATURE [Assembly::JointGroup] Joints001
  Group = -> [Joint007]
FEATURE [Assembly::AssemblyObject] Assembly001
  Group = -> [Joints001,Corps003,Corps006,Joint007]
  Origin = -> Origin018
  Placement = pos=(-21.035,5.00001,77.4903) rot=(0,1,0;0.697791rad)
  Type = Assembly
FEATURE [App::FeaturePython] Joint008  label="Revolute011"  # Assembly joint (typed FeaturePython)
  Angle = 0
  AngleMax = 0
  AngleMin = 0
  Detach1 = false
  Detach2 = false
  Distance = 0
  Distance2 = 0
  EnableAngleMax = false
  EnableAngleMin = false
  EnableLengthMax = false
  EnableLengthMin = false
  JointType = 1 (Revolute)
  LengthMax = 0
  LengthMin = 0
  Placement1 = pos=(33.0045,0,40.5366) rot=(1,0,0;1.5708rad)
  Placement2 = pos=(22.1303,-5,51.9285) rot=(1,0,0;1.5708rad)
  Reference1 = -> Assembly [Assembly001.Corps003.Edge17,Assembly001.Corps003.Edge17]
  Reference2 = -> Assembly [Body002.Edge18,Body002.Edge18]
  Suppressed = false
FEATURE [App::FeaturePython] Joint009  label="Revolute012"  # Assembly joint (typed FeaturePython)
  Angle = 0
  AngleMax = 0
  AngleMin = 0
  Detach1 = false
  Detach2 = false
  Distance = 0
  Distance2 = 0
  EnableAngleMax = false
  EnableAngleMin = false
  EnableLengthMax = false
  EnableLengthMin = false
  JointType = 1 (Revolute)
  LengthMax = 0
  LengthMin = 0
  Placement1 = pos=(33.0045,0,17.7064) rot=(1,0,0;1.5708rad)
  Placement2 = pos=(33.061,-5,17.7892) rot=(1,0,0;1.5708rad)
  Reference1 = -> Assembly [Assembly001.Corps003.Edge14,Assembly001.Corps003.Edge14]
  Reference2 = -> Assembly [Body004.Edge27,Body004.Edge27]
  Suppressed = false
FEATURE [App::Point] Origin021  label="Origine020"
  Role = Origin
FEATURE [App::Link] Body007  label="Corps007"
  LinkedObject = -> <external TestInsert1-1.FCStd>#Body
FEATURE [App::Link] Body008  label="Corps008"
  LinkPlacement = pos=(-4.1e-15,3.6e-15,-4.7e-15) rot=(0,-1,0;4.71239rad)
  LinkedObject = -> <external TestInsert1-1.FCStd>#Body001
  Placement = pos=(-4.1e-15,3.6e-15,-4.7e-15) rot=(0,-1,0;4.71239rad)
FEATURE [Assembly::AssemblyLink] Assembly002  label="Assembly"
  Group = -> [Body007,Body008]
  LinkedObject = -> <external TestInsert1-1.FCStd>#Assembly
  Origin = -> Origin020
  Placement = pos=(82.0261,-8,29.1925) rot=(0,1,0;0.730396rad)
  Rigid = true
FEATURE [App::FeaturePython] Joint010  label="Revolute014"  # Assembly joint (typed FeaturePython)
  Angle = 0
  AngleMax = 0
  AngleMin = 0
  Detach1 = false
  Detach2 = false
  Distance = 0
  Distance2 = 0
  EnableAngleMax = false
  EnableAngleMin = false
  EnableLengthMax = false
  EnableLengthMin = false
  JointType = 1 (Revolute)
  LengthMax = 0
  LengthMin = 0
  Placement1 = pos=(0,0,0) rot=(-1,0,0;4.71239rad)
  Placement2 = pos=(95.172,0,14.315) rot=(1,0,0;1.5708rad)
  Reference1 = -> Assembly [Assembly002.Body008.Edge2,Assembly002.Body008.Edge2]
  Reference2 = -> Assembly [Assembly001.Corps006.Edge2,Assembly001.Corps006.Edge2]
  Suppressed = false
FEATURE [Assembly::JointGroup] Joints
  Group = -> [GroundedJoint,Joint,Joint001,Joint002,Joint005,Joint006,Joint008,Joint009,Joint010]
FEATURE [Assembly::AssemblyObject] Assembly
  Group = -> [Joints,Body,Body001,Body002,Body004,Body005,GroundedJoint,Joint,Joint001,Joint002,Joint005,Joint006,Assembly001,Joint008,Joint009,Assembly002,Joint010]
  Origin = -> Origin
  Type = Assembly
